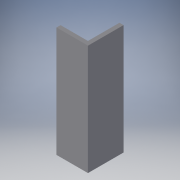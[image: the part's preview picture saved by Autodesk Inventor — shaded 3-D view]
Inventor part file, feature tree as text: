
AUTODESK INVENTOR PART (.ipt)
format: ipt  version: 2016 (Build 200138000, 138)  size: 90,112 bytes
history: native  units: in
note: dims shown in document units (in); Inventor stores cm internally (conversion verified against a paired STEP export)
features: extrude x1, sketch x1
ambient origin geometry x8: Origin, YZ Plane, XZ Plane, XY Plane, X Axis, Y Axis, Z Axis, Center Point
bodies: Solid1 (feature_tree)
feature tree (2):
  extrude  "Extrusion1"  Depth=0.13in
  sketch  "Sketch1"  dims[d0=1.0in d1=0.13in d2=1.0in d3=0.13in d4=3.5in d5=0.0in]
